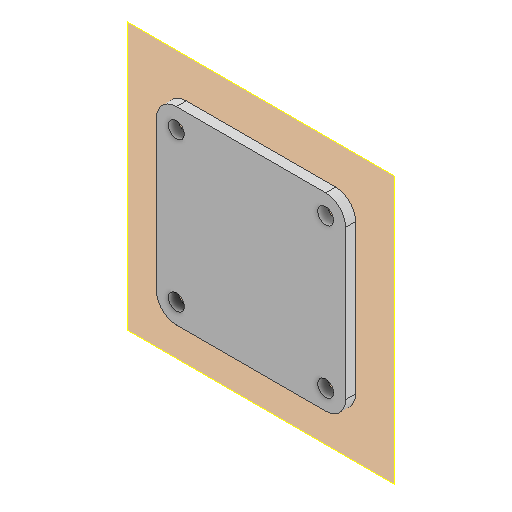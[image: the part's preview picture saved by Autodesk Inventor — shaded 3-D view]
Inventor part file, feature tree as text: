
AUTODESK INVENTOR PART (.ipt)
format: ipt  version: 2022 (Build 260153000, 153)  size: 122,880 bytes
history: native  units: mm
features: reference x5, other x3, plane x2, sketch x2, extrude x1, hole x1, projected_geometry x1
ambient origin geometry x8: Origin, YZ Plane, XZ Plane, XY Plane, X Axis, Y Axis, Z Axis, Center Point
bodies: Volumenkörper1 (feature_tree)
feature tree (15):
  plane  "Arbeitsebene1"
  extrude  "Extrusion1"  Depth=4.0mm
  plane  "Arbeitsebene2"
  hole  "Bohrung1"  [1 undecoded]
  sketch  "Skizze1"  dims[d0=4.0mm d1=4.0mm]
  reference  "Referenz1"
  sketch  "Skizze2"  dims[d2=2.0mm d3=0.0mm d4=3.2mm d5=6.0mm d6=4.0mm d7=2.0mm d8=90.0deg d9=8.0mm d10=20.594885mm]
  projected_geometry  "Projizierte Kontur1"
  reference  "Referenz2"
  reference  "Referenz3"
  reference  "Referenz4"
  reference  "Referenz5"
  other  "Assembly_Cube_SEEED_Xiao_Sense_Camera_v3.iam"
  other  "00_ESP32_XIAO_Adapter_base:1"
  other  "20_Cube_Insert_SEEED_Xiao_Sense_Camera:1"
note: 1 required parameter value undecoded (feature->parameter linkage not recoverable at this tier; creation-order binding heuristic only, values carry confidence <= 0.55)
